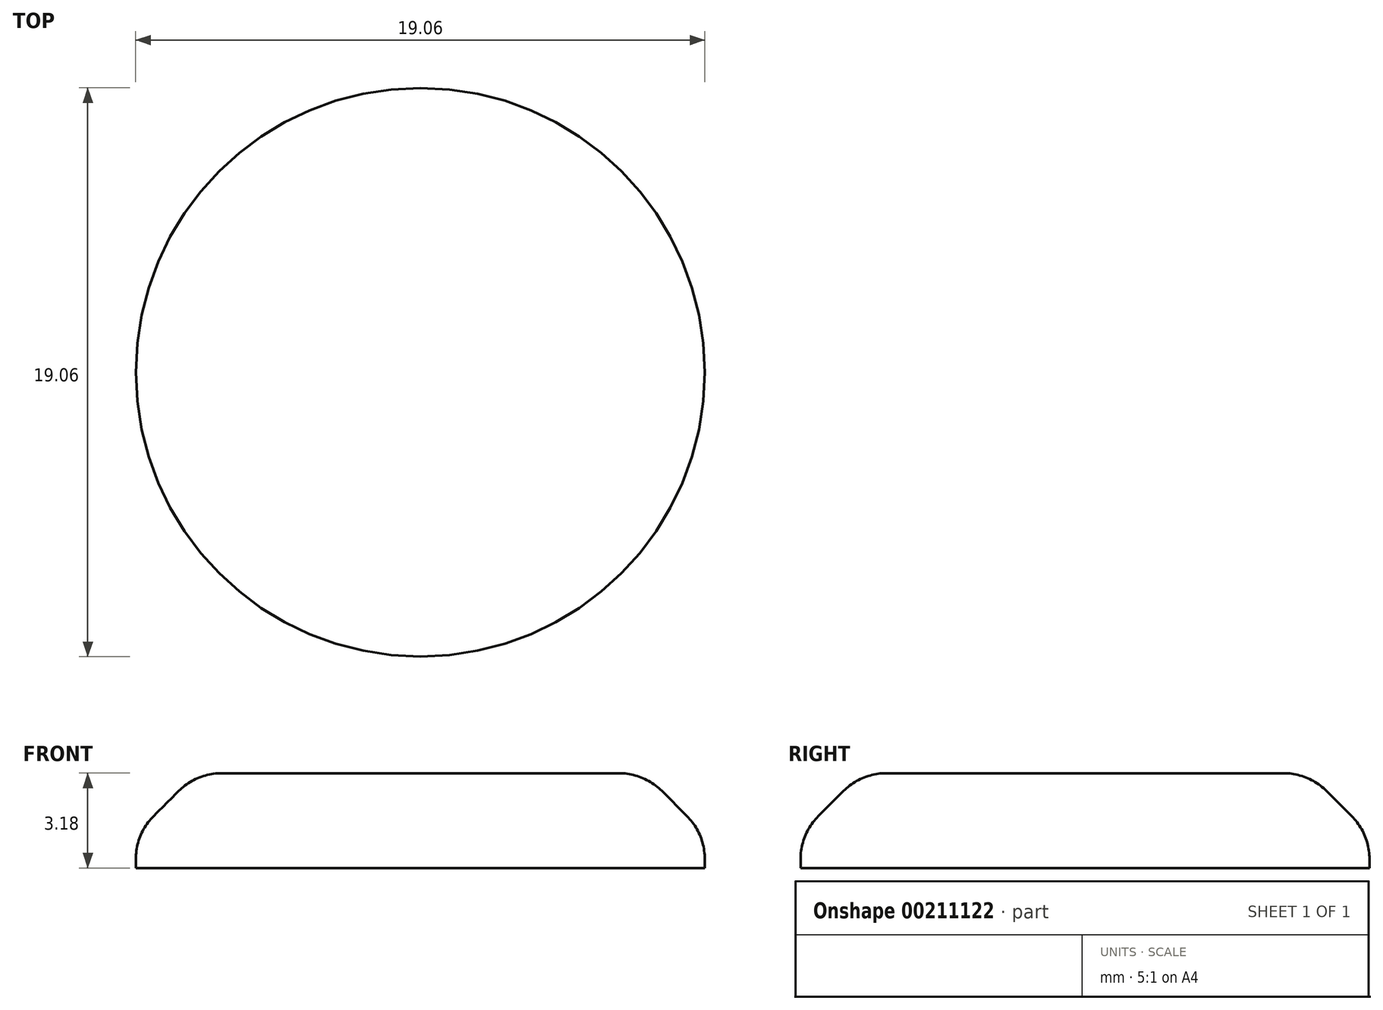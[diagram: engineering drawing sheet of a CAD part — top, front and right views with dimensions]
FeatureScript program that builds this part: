
annotation { "Feature Type Name" : "Feature", "Feature Type Description" : "" }
export const myFeature = defineFeature(function(context is Context, id is Id, definition is map)
    precondition{}
    {
        {
            var Q0;
            Q0=qCreatedBy(makeId("Top.planeOp"),FACE);
            var sketch = newSketch(context, id + "F0", { "sketchPlane" : qUnion([Q0])});
            skCircle(sketch, "E0", {"center": v(0, 0) * mm, "radius": 9.53 * mm});
            skSolve(sketch);
        }
        {
            var Q0;
            Q0=makeQuery(id+"F0.imprint","IMPRINT",FACE,{"disambiguationData":[TD([[makeQuery(id+"F0.imprint","IMPRINT",EDGE,{"derivedFrom":sQuery(id+"F0.wireOp",EDGE,"E0")}),1.0]])]});
            extrude(context, id + "F1", {"entities" : qUnion([Q0]), "depth" : 3.17 * mm});
        }
        {
            var Q0;
            Q0=makeQuery(id+"F1.opExtrude","CAP_EDGE",EDGE,{"disambiguationData":[OSD([sQuery(id+"F0.wireOp",EDGE,"E0")])],"isStart":false});
            chamfer(context, id + "F2", {"entities" : qUnion([Q0]), "width" : 2.03 * mm, "tangentPropagation" : true});
        }
        {
            var Q0;
            {var subQ0=sQuery(id+"F0.wireOp",EDGE,"E0");Q0=makeQuery(id+"F2.opChamfer","BLEND_EDGE",EDGE,{"blendedFrom":[makeQuery(id+"F1.opExtrude","CAP_EDGE",EDGE,{"disambiguationData":[OSD([subQ0])],"isStart":false}),makeQuery(id+"F1.opExtrude","CAP_FACE",FACE,{"disambiguationData":[OSD([subQ0])],"isStart":false})],"blendedInto":[makeQuery(id+"F1.opExtrude","CAP_FACE",FACE,{"disambiguationData":[OSD([subQ0])],"isStart":false})]});}
            var Q1;
            {var subQ0=sQuery(id+"F0.wireOp",EDGE,"E0");Q1=makeQuery(id+"F2.opChamfer","BLEND_EDGE",EDGE,{"blendedFrom":[makeQuery(id+"F1.opExtrude","CAP_EDGE",EDGE,{"disambiguationData":[OSD([subQ0])],"isStart":false}),makeQuery(id+"F1.opExtrude","SWEPT_FACE",FACE,{"disambiguationData":[OSD([subQ0])]})],"blendedInto":[makeQuery(id+"F1.opExtrude","SWEPT_FACE",FACE,{"disambiguationData":[OSD([subQ0])]})]});}
            fillet(context, id + "F3", {"entities" : qUnion([Q0, Q1]), "radius" : 2.03 * mm, "tangentPropagation" : true, "allowEdgeOverflow" : false});
        }
    });
